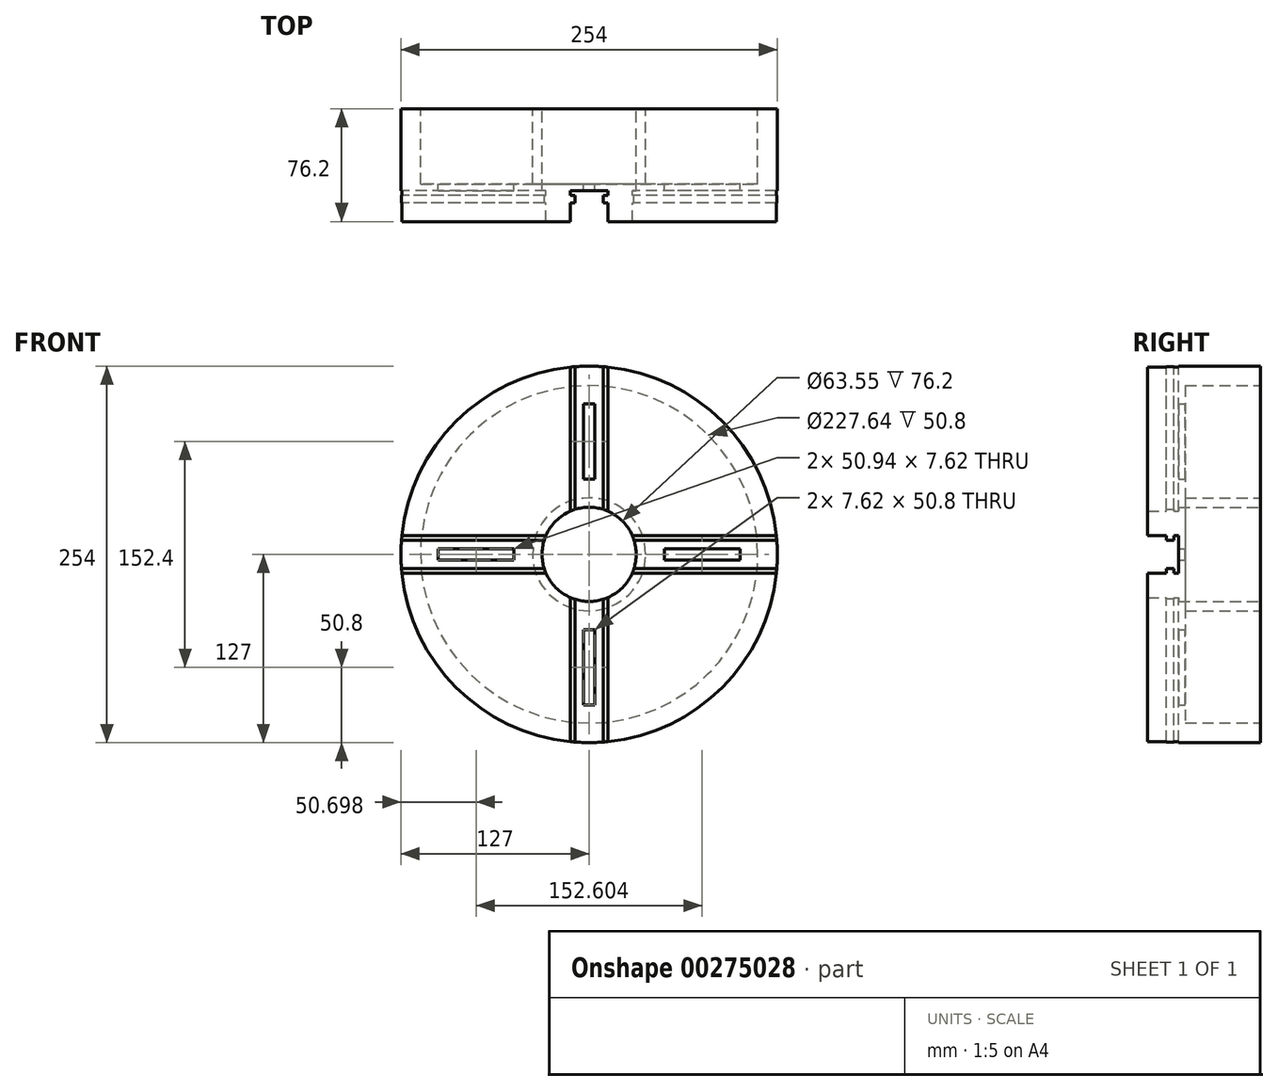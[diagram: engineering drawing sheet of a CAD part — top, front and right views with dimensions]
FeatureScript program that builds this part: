
annotation { "Feature Type Name" : "Feature", "Feature Type Description" : "" }
export const myFeature = defineFeature(function(context is Context, id is Id, definition is map)
    precondition{}
    {
        {
            var Q0;
            Q0=qCreatedBy(makeId("Front.planeOp"),FACE);
            var sketch = newSketch(context, id + "F0", { "sketchPlane" : qUnion([Q0])});
            skCircle(sketch, "E0", {"center": v(0, 0) * mm, "radius": 127 * mm});
            skCircle(sketch, "E1", {"center": v(0, 0) * mm, "radius": 31.77 * mm});
            skSolve(sketch);
        }
        {
            var Q0;
            Q0 = qSketchRegion(id + "F0", true);
            extrude(context, id + "F1", {"entities" : qUnion([Q0]), "depth" : 76.2 * mm});
        }
        {
            var Q0;
            Q0=qCreatedBy(makeId("Right.planeOp"),FACE);
            var sketch = newSketch(context, id + "F2", { "sketchPlane" : qUnion([Q0])});
            skLineSegment(sketch, "E2.bottom", {"start": v(-76.2, 12.7) * mm, "end": v(-63.5, 12.7) * mm});
            skLineSegment(sketch, "E2.top", {"start": v(-76.2, -12.7) * mm, "end": v(-63.5, -12.7) * mm});
            skLineSegment(sketch, "E2.left", {"start": v(-76.2, 12.7) * mm, "end": v(-76.2, -12.7) * mm});
            skLineSegment(sketch, "E2.right", {"start": v(-63.5, 12.7) * mm, "end": v(-63.5, 9.53) * mm});
            skPoint(sketch, "E2.middle", {"position": v(-69.85, 0) * mm});
            skLineSegment(sketch, "E3.bottom", {"start": v(-58.42, 9.53) * mm, "end": v(-63.5, 9.53) * mm});
            skLineSegment(sketch, "E3.top", {"start": v(-58.42, -9.53) * mm, "end": v(-63.5, -9.53) * mm});
            skPoint(sketch, "E3.middle", {"position": v(-63.5, 0) * mm});
            skPoint(sketch, "E3.right.end.orphan", {"position": v(-68.58, -9.53) * mm});
            skPoint(sketch, "E3.right.start.orphan", {"position": v(-68.58, 9.53) * mm});
            skLineSegment(sketch, "E4.trimOffspring", {"start": v(-63.5, -9.53) * mm, "end": v(-63.5, -12.7) * mm});
            skLineSegment(sketch, "E5", {"start": v(-58.42, 9.53) * mm, "end": v(-58.42, 12.7) * mm});
            skLineSegment(sketch, "E6", {"start": v(-58.42, 12.7) * mm, "end": v(-55.25, 12.7) * mm});
            skLineSegment(sketch, "E7", {"start": v(-55.25, 12.7) * mm, "end": v(-55.25, -12.7) * mm});
            skLineSegment(sketch, "E8", {"start": v(-55.25, -12.7) * mm, "end": v(-58.42, -12.7) * mm});
            skLineSegment(sketch, "E9", {"start": v(-58.42, -12.7) * mm, "end": v(-58.42, -9.53) * mm});
            skSolve(sketch);
        }
        {
            var Q0;
            Q0=makeQuery(id+"F2.imprint","IMPRINT",FACE,{"disambiguationData":[TD([[makeQuery(id+"F2.imprint","IMPRINT",EDGE,{"derivedFrom":sQuery(id+"F2.wireOp",EDGE,"E2.bottom")}),-1.0]])]});
            extrude(context, id + "F3", {"entities" : qUnion([Q0]), "operationType" : NewBodyOperationType.REMOVE, "endBound" : BoundingType.SYMMETRIC, "depth" : 254 * mm});
        }
        {
            var Q0;
            Q0=qCreatedBy(makeId("Top.planeOp"),FACE);
            var sketch = newSketch(context, id + "F4", { "sketchPlane" : qUnion([Q0])});
            skLineSegment(sketch, "E10.bottom", {"start": v(12.7, -63.5) * mm, "end": v(9.53, -63.5) * mm});
            skLineSegment(sketch, "E10.top", {"start": v(12.7, -76.2) * mm, "end": v(-12.7, -76.2) * mm});
            skLineSegment(sketch, "E10.left", {"start": v(12.7, -63.5) * mm, "end": v(12.7, -76.2) * mm});
            skLineSegment(sketch, "E10.right", {"start": v(-12.7, -63.5) * mm, "end": v(-12.7, -76.2) * mm});
            skPoint(sketch, "E10.middle", {"position": v(0, -69.85) * mm});
            skLineSegment(sketch, "E11.left", {"start": v(9.52, -58.42) * mm, "end": v(9.53, -63.5) * mm});
            skLineSegment(sketch, "E11.right", {"start": v(-9.53, -58.42) * mm, "end": v(-9.53, -63.5) * mm});
            skPoint(sketch, "E11.middle", {"position": v(0, -63.5) * mm});
            skLineSegment(sketch, "E12.trimOffspring", {"start": v(-9.53, -63.5) * mm, "end": v(-12.7, -63.5) * mm});
            skPoint(sketch, "E13.orphan", {"position": v(-9.52, -68.58) * mm});
            skPoint(sketch, "E14.orphan", {"position": v(9.53, -68.58) * mm});
            skLineSegment(sketch, "E15.bottom", {"start": v(-12.7, -58.42) * mm, "end": v(-9.53, -58.42) * mm});
            skLineSegment(sketch, "E15.top", {"start": v(-12.7, -55.25) * mm, "end": v(12.73, -55.25) * mm});
            skLineSegment(sketch, "E15.left", {"start": v(-12.7, -58.42) * mm, "end": v(-12.7, -55.25) * mm});
            skLineSegment(sketch, "E15.right", {"start": v(12.73, -58.42) * mm, "end": v(12.73, -55.25) * mm});
            skLineSegment(sketch, "E16.trimOffspring", {"start": v(9.52, -58.42) * mm, "end": v(12.73, -58.42) * mm});
            skSolve(sketch);
        }
        {
            var Q0;
            Q0 = qSketchRegion(id + "F4", true);
            extrude(context, id + "F5", {"entities" : qUnion([Q0]), "operationType" : NewBodyOperationType.REMOVE, "endBound" : BoundingType.SYMMETRIC, "oppositeDirection" : true, "depth" : 254 * mm});
        }
        {
            var Q0;
            Q0=makeQuery(id+"F1.opExtrude","CAP_FACE",FACE,{"disambiguationData":[OSD([sQuery(id+"F0.wireOp",EDGE,"E0"),sQuery(id+"F0.wireOp",EDGE,"E1")])],"isStart":true});
            var sketch = newSketch(context, id + "F6", { "sketchPlane" : qUnion([Q0])});
            skCircle(sketch, "E17", {"center": v(0, 0) * mm, "radius": 113.82 * mm});
            skCircle(sketch, "E18", {"center": v(0, 0) * mm, "radius": 38.1 * mm});
            skSolve(sketch);
        }
        {
            var Q0;
            Q0 = qSketchRegion(id + "F6", true);
            extrude(context, id + "F7", {"entities" : qUnion([Q0]), "operationType" : NewBodyOperationType.REMOVE, "oppositeDirection" : true, "depth" : 50.8 * mm});
        }
        {
            var Q0;
            Q0=qCreatedBy(makeId("Front.planeOp"),FACE);
            var sketch = newSketch(context, id + "F8", { "sketchPlane" : qUnion([Q0])});
            skPoint(sketch, "E19.middle", {"position": v(0, 76.2) * mm});
            skLineSegment(sketch, "E20.bottom", {"start": v(101.77, -3.81) * mm, "end": v(50.83, -3.81) * mm});
            skLineSegment(sketch, "E20.top", {"start": v(101.77, 3.81) * mm, "end": v(50.83, 3.81) * mm});
            skLineSegment(sketch, "E20.left", {"start": v(101.77, -3.81) * mm, "end": v(101.77, 3.81) * mm});
            skLineSegment(sketch, "E20.right", {"start": v(50.83, -3.81) * mm, "end": v(50.83, 3.81) * mm});
            skPoint(sketch, "E20.middle", {"position": v(76.3, 0) * mm});
            skLineSegment(sketch, "E21.bottom", {"start": v(-101.77, -3.81) * mm, "end": v(-50.83, -3.81) * mm});
            skLineSegment(sketch, "E21.top", {"start": v(-101.77, 3.8) * mm, "end": v(-50.83, 3.8) * mm});
            skLineSegment(sketch, "E21.left", {"start": v(-101.77, -3.81) * mm, "end": v(-101.77, 3.8) * mm});
            skLineSegment(sketch, "E21.right", {"start": v(-50.83, -3.81) * mm, "end": v(-50.83, 3.8) * mm});
            skPoint(sketch, "E21.middle", {"position": v(-76.3, 0) * mm});
            skPoint(sketch, "E22.middle", {"position": v(0, -76.2) * mm});
            skPoint(sketch, "E23.orphan", {"position": v(2.54, -101.6) * mm});
            skPoint(sketch, "E24.orphan", {"position": v(-2.54, -101.6) * mm});
            skPoint(sketch, "E22.top.end.orphan", {"position": v(-2.54, -50.8) * mm});
            skPoint(sketch, "E22.top.start.orphan", {"position": v(2.54, -50.8) * mm});
            skLineSegment(sketch, "E25.bottom", {"start": v(-3.8, -101.6) * mm, "end": v(3.81, -101.6) * mm});
            skLineSegment(sketch, "E25.top", {"start": v(-3.81, -50.8) * mm, "end": v(3.8, -50.8) * mm});
            skLineSegment(sketch, "E25.left", {"start": v(-3.8, -101.6) * mm, "end": v(-3.81, -50.8) * mm});
            skLineSegment(sketch, "E25.right", {"start": v(3.81, -101.6) * mm, "end": v(3.8, -50.8) * mm});
            skPoint(sketch, "E19.top.end.orphan", {"position": v(-2.54, 101.6) * mm});
            skPoint(sketch, "E26.orphan", {"position": v(2.54, 101.6) * mm});
            skPoint(sketch, "E19.bottom.end.orphan", {"position": v(-2.54, 50.8) * mm});
            skPoint(sketch, "E19.bottom.start.orphan", {"position": v(2.54, 50.8) * mm});
            skLineSegment(sketch, "E27.bottom", {"start": v(-3.8, 50.8) * mm, "end": v(3.81, 50.8) * mm});
            skLineSegment(sketch, "E27.top", {"start": v(-3.8, 101.6) * mm, "end": v(3.81, 101.6) * mm});
            skLineSegment(sketch, "E27.left", {"start": v(-3.8, 50.8) * mm, "end": v(-3.8, 101.6) * mm});
            skLineSegment(sketch, "E27.right", {"start": v(3.81, 50.8) * mm, "end": v(3.81, 101.6) * mm});
            skSolve(sketch);
        }
        {
            var Q0;
            Q0 = qSketchRegion(id + "F8", true);
            extrude(context, id + "F9", {"entities" : qUnion([Q0]), "operationType" : NewBodyOperationType.REMOVE, "depth" : 76.2 * mm});
        }
    });
